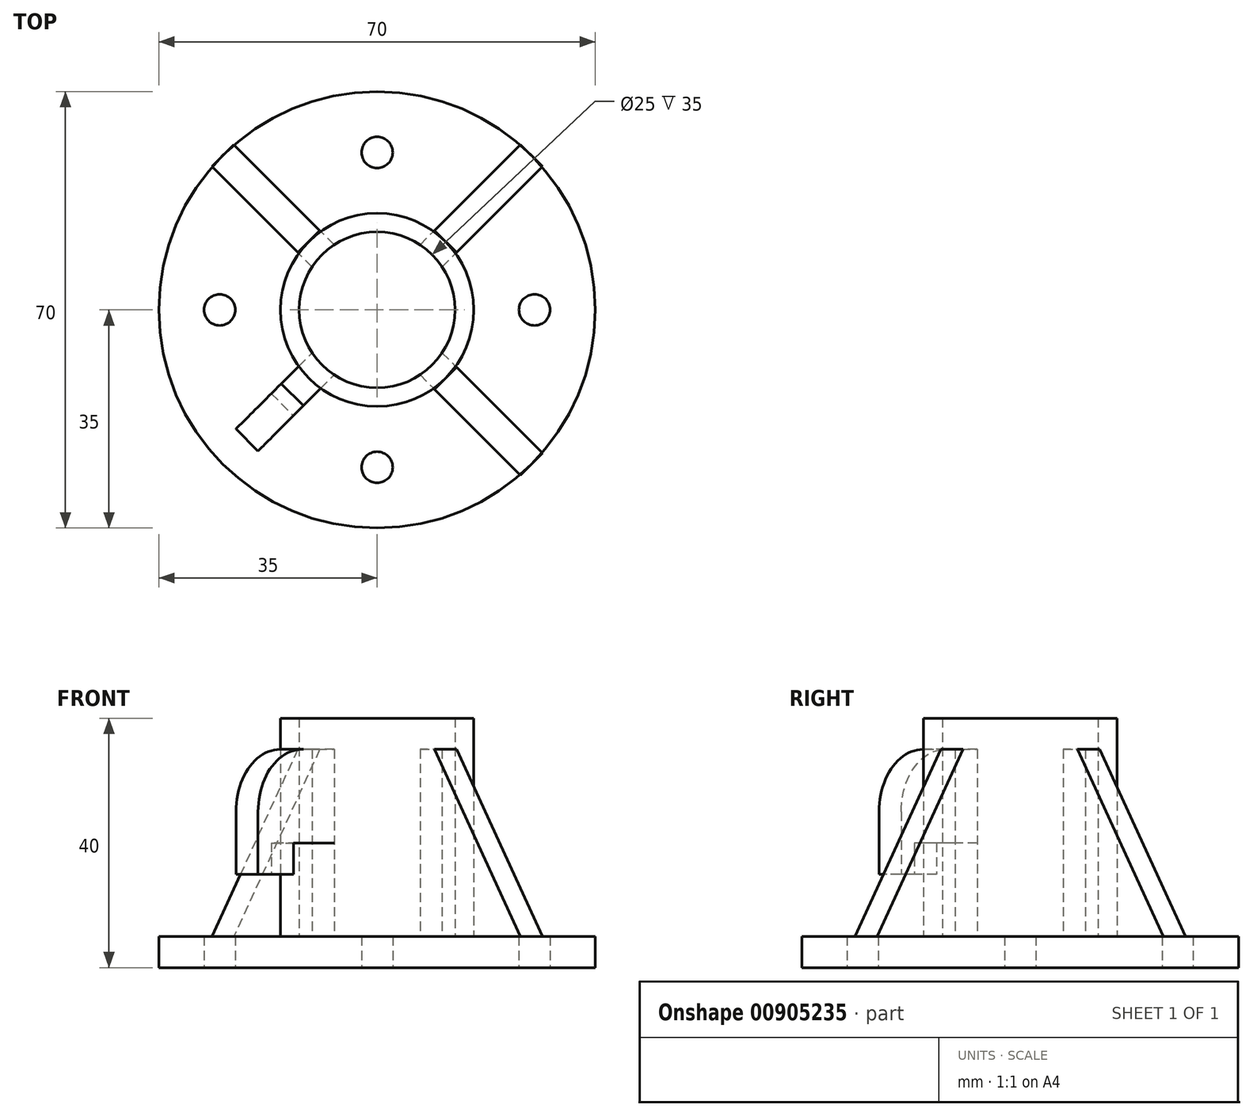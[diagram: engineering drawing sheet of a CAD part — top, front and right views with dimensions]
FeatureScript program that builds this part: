
annotation { "Feature Type Name" : "Feature", "Feature Type Description" : "" }
export const myFeature = defineFeature(function(context is Context, id is Id, definition is map)
    precondition{}
    {
        {
            assignVariable(context, id + "F0", {"name" : "zakladna_vyska", "anyValue" : 5 * mm});
        }
        {
            assignVariable(context, id + "F1", {"name" : "vyska_tyc", "anyValue" : 40 * mm});
        }
        {
            assignVariable(context, id + "F2", {"name" : "podpera_sila", "anyValue" : 5 * mm});
        }
        {
            var Q0;
            Q0=qCreatedBy(makeId("Top.planeOp"),FACE);
            var sketch = newSketch(context, id + "F3", { "sketchPlane" : qUnion([Q0])});
            skCircle(sketch, "E0", {"center": v(0, 0) * mm, "radius": 35 * mm});
            skCircle(sketch, "E1", {"center": v(0, 25.25) * mm, "radius": 2.5 * mm});
            skCircle(sketch, "E2", {"center": v(0, 0) * mm, "radius": 12.5 * mm});
            skCircle(sketch, "E3.0", {"center": v(0, 0) * mm, "radius": 15.5 * mm});
            skCircle(sketch, "E4.1.0", {"center": v(-25.25, 0) * mm, "radius": 2.5 * mm});
            skCircle(sketch, "E4.2.0", {"center": v(0, -25.25) * mm, "radius": 2.5 * mm});
            skCircle(sketch, "E4.3.0", {"center": v(25.25, 0) * mm, "radius": 2.5 * mm});
            skSolve(sketch);
        }
        {
            var Q0;
            Q0=makeQuery(id+"F3.imprint","IMPRINT",FACE,{"disambiguationData":[TD([[makeQuery(id+"F3.imprint","IMPRINT",EDGE,{"derivedFrom":sQuery(id+"F3.wireOp",EDGE,"E0")}),1.0]])]});
            extrude(context, id + "F4", {"entities" : qUnion([Q0]), "depth" : getVariable(context, 'zakladna_vyska'), "offsetDistance" : 25 * mm});
        }
        {
            var Q0;
            Q0=makeQuery(id+"F3.imprint","IMPRINT",FACE,{"disambiguationData":[TD([[makeQuery(id+"F3.imprint","IMPRINT",EDGE,{"derivedFrom":sQuery(id+"F3.wireOp",EDGE,"E2")}),-1.0]])]});
            var Q1;
            Q1=makeQuery(id+"F3.imprint","IMPRINT",FACE,{"disambiguationData":[TD([[makeQuery(id+"F3.imprint","IMPRINT",EDGE,{"derivedFrom":sQuery(id+"F3.wireOp",EDGE,"E2")}),1.0]])]});
            extrude(context, id + "F5", {"entities" : qUnion([Q0, Q1]), "operationType" : NewBodyOperationType.ADD, "depth" : getVariable(context, 'vyska_tyc'), "offsetDistance" : 25 * mm});
        }
        {
            var Q0;
            Q0=qCreatedBy(makeId("Right.planeOp"),FACE);
            var sketch = newSketch(context, id + "F6", { "sketchPlane" : qUnion([Q0])});
            skLineSegment(sketch, "E5", {"start": v(-35, 5) * mm, "end": v(0, 5) * mm});
            skLineSegment(sketch, "E6", {"start": v(0, 5) * mm, "end": v(0, 35) * mm});
            skLineSegment(sketch, "E7", {"start": v(0, 35) * mm, "end": v(-15.5, 35) * mm});
            skLineSegment(sketch, "E8", {"start": v(-15.5, 35) * mm, "end": v(-35, 5) * mm});
            skLineSegment(sketch, "E9", {"start": v(0, 20) * mm, "end": v(21.5, 20) * mm});
            skLineSegment(sketch, "E10", {"start": v(21.5, 20) * mm, "end": v(21.5, 14.96) * mm});
            skLineSegment(sketch, "E11", {"start": v(21.5, 14.96) * mm, "end": v(29.5, 14.96) * mm});
            skLineSegment(sketch, "E12", {"start": v(29.5, 25) * mm, "end": v(29.5, 14.96) * mm});
            skPoint(sketch, "E13.visualSharp", {"position": v(29.5, 35) * mm});
            skArc(sketch, "E13.filletArc", {"start": v(29.5, 25) * mm, "mid": v(26.48, 32.16) * mm, "end": v(19.25, 35) * mm});
            skLineSegment(sketch, "E14", {"start": v(19.25, 35) * mm, "end": v(0, 35) * mm});
            skLineSegment(sketch, "E15", {"start": v(0, 35) * mm, "end": v(0, 20) * mm});
            skSolve(sketch);
        }
        {
            var Q0;
            Q0=makeQuery(id+"F6.imprint","IMPRINT",FACE,{"disambiguationData":[TD([[makeQuery(id+"F6.imprint","IMPRINT",EDGE,{"derivedFrom":sQuery(id+"F6.wireOp",EDGE,"E5")}),1.0]])]});
            extrude(context, id + "F7", {"entities" : qUnion([Q0]), "depth" : getVariable(context, 'podpera_sila'), "offsetDistance" : 25 * mm, "symmetric" : true});
        }
        {
            var Q0;
            Q0=makeQuery(id+"F7.opExtrude","SWEPT_BODY",BODY,{"disambiguationData":[OSD([sQuery(id+"F6.wireOp",EDGE,"E5"),sQuery(id+"F6.wireOp",EDGE,"E6"),sQuery(id+"F6.wireOp",EDGE,"E7"),sQuery(id+"F6.wireOp",EDGE,"E8"),sQuery(id+"F6.wireOp",EDGE,"E15")])]});
            var Q1;
            Q1=sQuery(id+"F3.wireOp",EDGE,"E3.0");
            transform(context, id + "F8", {"entities" : qUnion([Q0]), "transformType" : TransformType.ROTATION, "transformAxis" : qUnion([Q1]), "angle" : 45 * degree, "makeCopy" : false});
        }
        {
            var Q0;
            Q0=makeQuery(id+"F7.opExtrude","SWEPT_BODY",BODY,{"disambiguationData":[OSD([sQuery(id+"F6.wireOp",EDGE,"E5"),sQuery(id+"F6.wireOp",EDGE,"E6"),sQuery(id+"F6.wireOp",EDGE,"E7"),sQuery(id+"F6.wireOp",EDGE,"E8"),sQuery(id+"F6.wireOp",EDGE,"E15")])]});
            var Q1;
            Q1=sQuery(id+"F3.wireOp",EDGE,"E3.0");
            transform(context, id + "F9", {"entities" : qUnion([Q0]), "transformType" : TransformType.ROTATION, "transformAxis" : qUnion([Q1]), "angle" : 90 * degree, "makeCopy" : true});
        }
        {
            var Q0;
            Q0=makeQuery(id+"F9.opPattern","COPY",BODY,{"derivedFrom":makeQuery(id+"F7.opExtrude","SWEPT_BODY",BODY,{"disambiguationData":[OSD([sQuery(id+"F6.wireOp",EDGE,"E5"),sQuery(id+"F6.wireOp",EDGE,"E6"),sQuery(id+"F6.wireOp",EDGE,"E7"),sQuery(id+"F6.wireOp",EDGE,"E8"),sQuery(id+"F6.wireOp",EDGE,"E15")])]}),"instanceName":"1"});
            var Q1;
            Q1=sQuery(id+"F3.wireOp",EDGE,"E3.0");
            var Q2;
            Q2=sQuery(id+"F3.wireOp",EDGE,"E3.0");
            transform(context, id + "F10", {"entities" : qUnion([Q0]), "transformType" : TransformType.ROTATION, "transformAxis" : qUnion([Q2]), "angle" : 90 * degree, "makeCopy" : true});
        }
        {
            var Q0;
            Q0=makeQuery(id+"F6.imprint","IMPRINT",FACE,{"disambiguationData":[TD([[makeQuery(id+"F6.imprint","IMPRINT",EDGE,{"derivedFrom":sQuery(id+"F6.wireOp",EDGE,"E9")}),1.0]])]});
            extrude(context, id + "F11", {"entities" : qUnion([Q0]), "depth" : getVariable(context, 'podpera_sila'), "offsetDistance" : 25 * mm, "symmetric" : true});
        }
        {
            var Q0;
            Q0=makeQuery(id+"F11.opExtrude","SWEPT_BODY",BODY,{"disambiguationData":[OSD([sQuery(id+"F6.wireOp",EDGE,"E9"),sQuery(id+"F6.wireOp",EDGE,"E10"),sQuery(id+"F6.wireOp",EDGE,"E11"),sQuery(id+"F6.wireOp",EDGE,"E12"),sQuery(id+"F6.wireOp",EDGE,"E13.filletArc"),sQuery(id+"F6.wireOp",EDGE,"E14"),sQuery(id+"F6.wireOp",EDGE,"E15")])]});
            var Q1;
            Q1=sQuery(id+"F3.wireOp",EDGE,"E3.0");
            transform(context, id + "F12", {"entities" : qUnion([Q0]), "transformType" : TransformType.ROTATION, "transformAxis" : qUnion([Q1]), "angle" : 135 * degree, "makeCopy" : false});
        }
        {
            var Q0;
            Q0=qCreatedBy(makeId("Top.planeOp"),FACE);
            cPlane(context, id + "F13", {"entities" : qUnion([Q0]), "cplaneType" : CPlaneType.OFFSET, "offset" : getVariable(context, 'zakladna_vyska'), "width" : 150 * mm, "height" : 150 * mm});
        }
        {
            var Q0;
            Q0=qCreatedBy(id+"F13.planeOp",FACE);
            var sketch = newSketch(context, id + "F14", { "sketchPlane" : qUnion([Q0])});
            skCircle(sketch, "E16", {"center": v(0, 0) * mm, "radius": 12.5 * mm});
            skSolve(sketch);
        }
        {
            var Q0;
            Q0=makeQuery(id+"F14.imprint","IMPRINT",FACE,{"disambiguationData":[TD([[makeQuery(id+"F14.imprint","IMPRINT",EDGE,{"derivedFrom":sQuery(id+"F14.wireOp",EDGE,"E16")}),1.0]])]});
            extrude(context, id + "F15", {"entities" : qUnion([Q0]), "operationType" : NewBodyOperationType.REMOVE, "depth" : getVariable(context, 'vyska_tyc'), "offsetDistance" : 25 * mm});
        }
    });
